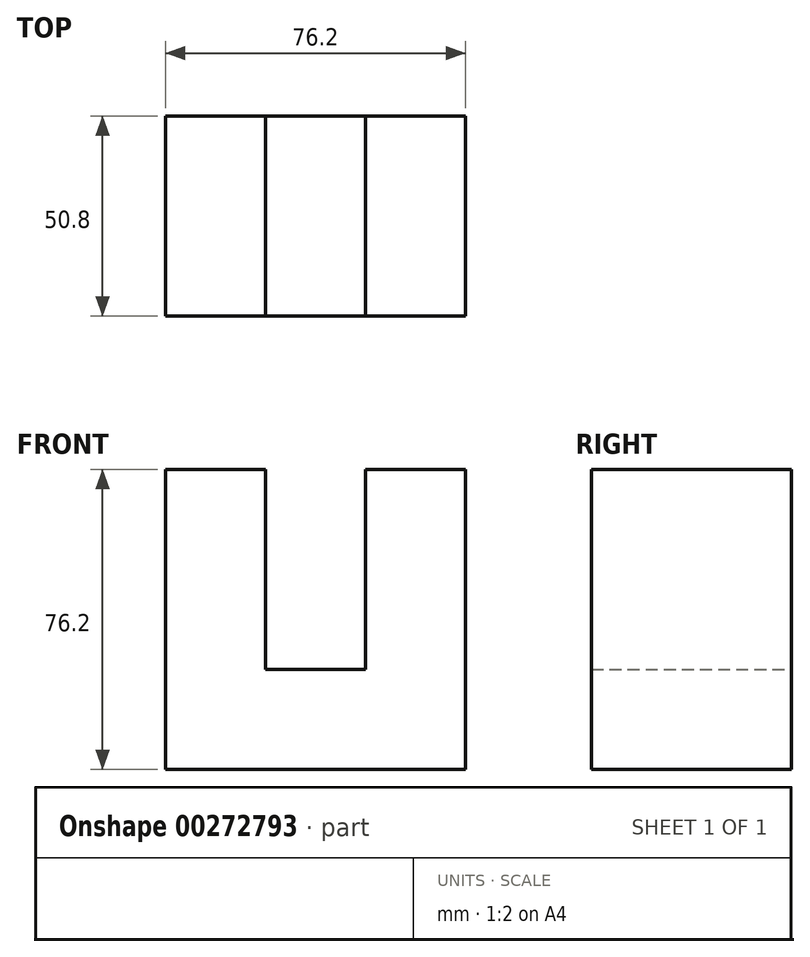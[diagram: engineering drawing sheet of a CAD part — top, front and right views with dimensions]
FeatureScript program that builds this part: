
annotation { "Feature Type Name" : "Feature", "Feature Type Description" : "" }
export const myFeature = defineFeature(function(context is Context, id is Id, definition is map)
    precondition{}
    {
        {
            var Q0;
            Q0=qCreatedBy(makeId("Front.planeOp"),FACE);
            var sketch = newSketch(context, id + "F0", { "sketchPlane" : qUnion([Q0])});
            skLineSegment(sketch, "E0", {"start": v(0, 0) * mm, "end": v(-76.2, 0) * mm});
            skLineSegment(sketch, "E1", {"start": v(-76.2, 0) * mm, "end": v(-76.2, 76.2) * mm});
            skLineSegment(sketch, "E2", {"start": v(-76.2, 76.2) * mm, "end": v(-50.8, 76.2) * mm});
            skLineSegment(sketch, "E3", {"start": v(-50.8, 76.2) * mm, "end": v(-50.8, 25.4) * mm});
            skLineSegment(sketch, "E4", {"start": v(-50.8, 25.4) * mm, "end": v(-25.4, 25.4) * mm});
            skPoint(sketch, "E5.end.orphan", {"position": v(-27.23, 76.2) * mm});
            skLineSegment(sketch, "E6", {"start": v(-25.4, 25.4) * mm, "end": v(-25.4, 76.2) * mm});
            skLineSegment(sketch, "E7", {"start": v(-25.4, 76.2) * mm, "end": v(0, 76.2) * mm});
            skLineSegment(sketch, "E8", {"start": v(0, 76.2) * mm, "end": v(0, 0) * mm});
            skSolve(sketch);
        }
        {
            var Q0;
            Q0 = qSketchRegion(id + "F0", true);
            extrude(context, id + "F1", {"entities" : qUnion([Q0]), "depth" : 50.8 * mm});
        }
    });
